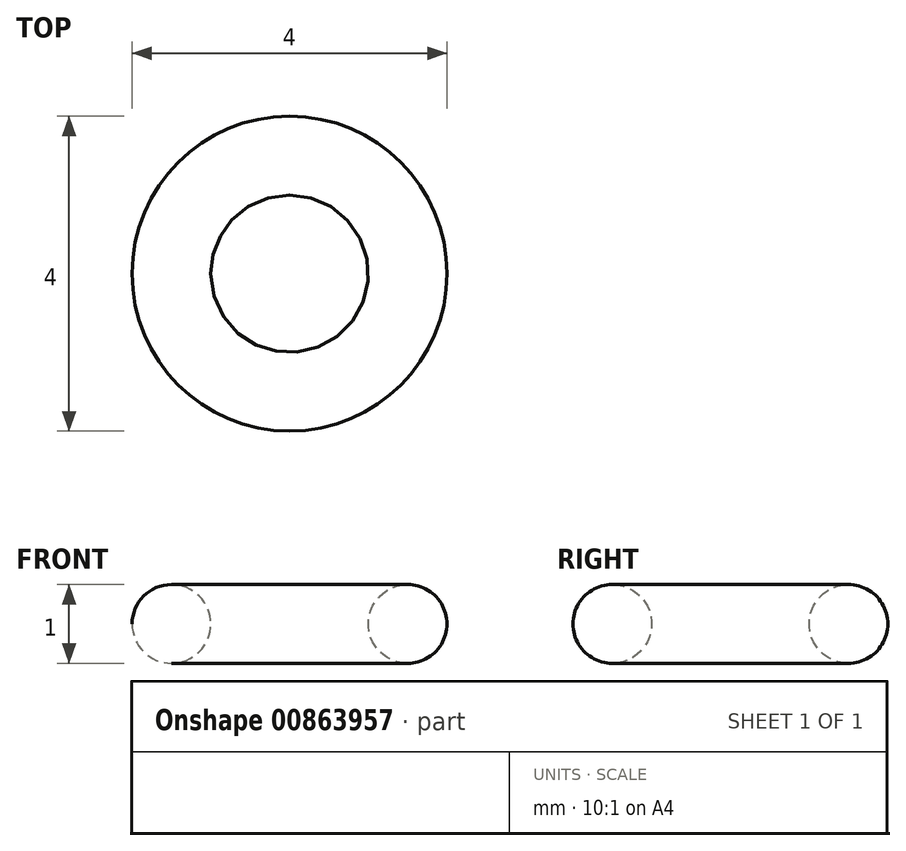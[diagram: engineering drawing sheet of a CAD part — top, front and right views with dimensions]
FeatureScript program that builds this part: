
annotation { "Feature Type Name" : "Feature", "Feature Type Description" : "" }
export const myFeature = defineFeature(function(context is Context, id is Id, definition is map)
    precondition{}
    {
        {
            var Q0;
            Q0=qCreatedBy(makeId("Front.planeOp"),FACE);
            var sketch = newSketch(context, id + "F0", { "sketchPlane" : qUnion([Q0])});
            skCircle(sketch, "E0", {"center": v(-1.5, 0) * mm, "radius": 0.5 * mm});
            skSolve(sketch);
        }
        {
            var Q0;
            Q0=qCreatedBy(makeId("Front.planeOp"),FACE);
            var sketch = newSketch(context, id + "F1", { "sketchPlane" : qUnion([Q0])});
            skLineSegment(sketch, "E1", {"start": v(0, 0) * mm, "end": v(0, 22.55) * mm});
            skSolve(sketch);
        }
        {
            var Q0;
            Q0=makeQuery(id+"F0.imprint","IMPRINT",FACE,{"disambiguationData":[TD([[makeQuery(id+"F0.imprint","IMPRINT",EDGE,{"derivedFrom":sQuery(id+"F0.wireOp",EDGE,"E0")}),1.0]])]});
            var Q1;
            Q1=sQuery(id+"F1.wireOp",EDGE,"E1");
            revolve(context, id + "F2", {"surfaceOperationType" : NewSurfaceOperationType.NEW, "entities" : qUnion([Q0]), "axis" : qUnion([Q1]), "revolveType" : RevolveType.FULL});
        }
    });
